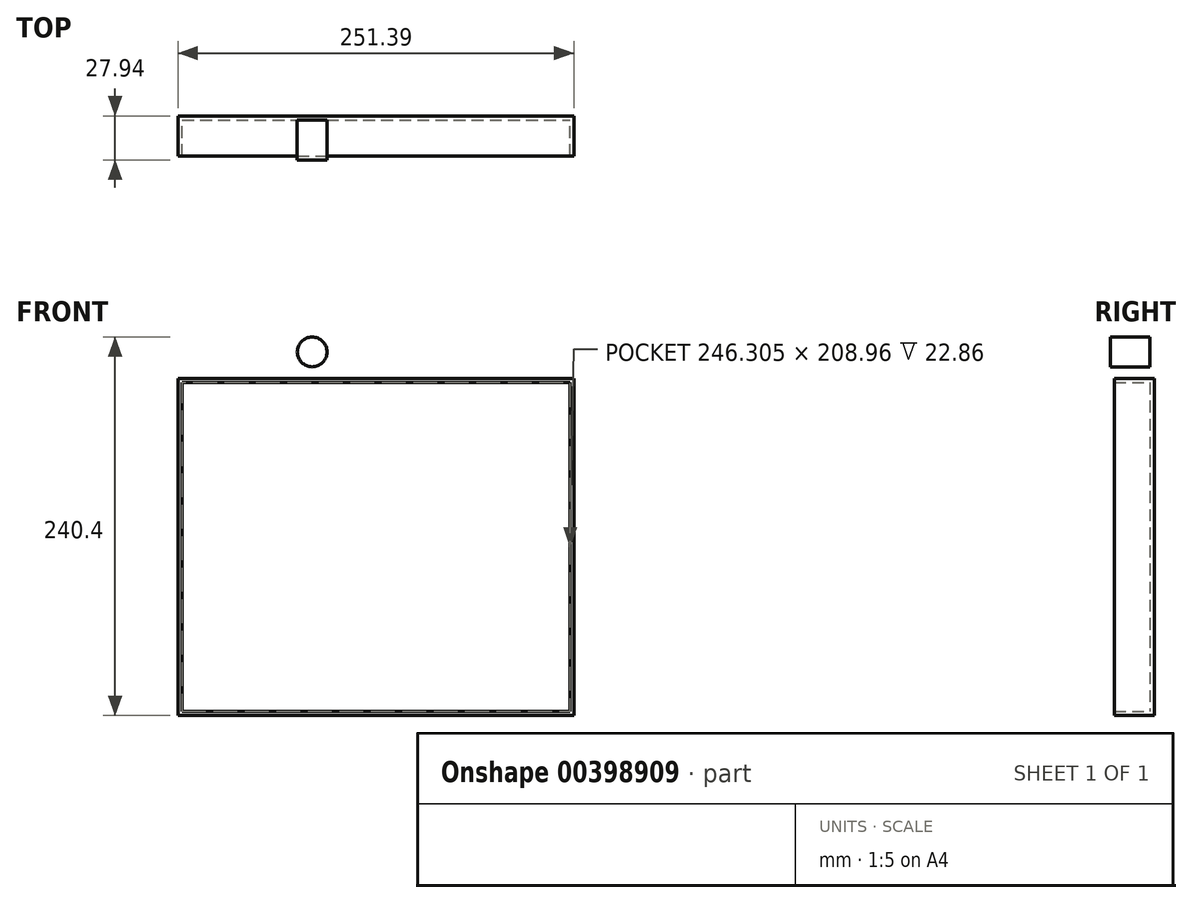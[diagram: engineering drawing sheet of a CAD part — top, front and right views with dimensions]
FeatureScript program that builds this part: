
annotation { "Feature Type Name" : "Feature", "Feature Type Description" : "" }
export const myFeature = defineFeature(function(context is Context, id is Id, definition is map)
    precondition{}
    {
        {
            var Q0;
            Q0=qCreatedBy(makeId("Front.planeOp"),FACE);
            var sketch = newSketch(context, id + "F0", { "sketchPlane" : qUnion([Q0])});
            skLineSegment(sketch, "E0.bottom", {"start": v(-605.9, 21.92) * mm, "end": v(-354.52, 21.92) * mm});
            skLineSegment(sketch, "E0.top", {"start": v(-605.9, -192.12) * mm, "end": v(-354.52, -192.12) * mm});
            skLineSegment(sketch, "E0.left", {"start": v(-605.9, 21.92) * mm, "end": v(-605.9, -192.12) * mm});
            skLineSegment(sketch, "E0.right", {"start": v(-354.52, 21.92) * mm, "end": v(-354.52, -192.12) * mm});
            skSolve(sketch);
        }
        {
            var Q0;
            Q0=makeQuery(id+"F0.imprint","IMPRINT",FACE,{"disambiguationData":[TD([[makeQuery(id+"F0.imprint","IMPRINT",EDGE,{"derivedFrom":sQuery(id+"F0.wireOp",EDGE,"E0.bottom")}),-1.0]])]});
            var sketch = newSketch(context, id + "F1", { "sketchPlane" : qUnion([Q0])});
            skLineSegment(sketch, "E1", {"start": v(-567.45, 7.98) * mm, "end": v(-581.38, -26.02) * mm});
            skLineSegment(sketch, "E2", {"start": v(-567.45, 7.98) * mm, "end": v(-552.4, -26.02) * mm});
            skLineSegment(sketch, "E3", {"start": v(-574.42, -9.02) * mm, "end": v(-559.92, -9.02) * mm});
            skLineSegment(sketch, "E4", {"start": v(-540.14, 7.98) * mm, "end": v(-540.14, -26.02) * mm});
            skLineSegment(sketch, "E5", {"start": v(-540.14, 7.98) * mm, "end": v(-517.28, -26.02) * mm});
            skLineSegment(sketch, "E6", {"start": v(-518.95, 7.98) * mm, "end": v(-517.28, -26.02) * mm});
            skLineSegment(sketch, "E7", {"start": v(-500, 7.98) * mm, "end": v(-500, -26.02) * mm});
            skFitSpline(sketch, "E8", {"points": [v(-500, 7.98) * mm, v(-476.6, -7.07) * mm, v(-500, -26.02) * mm], "startDerivative": vector(70.72, -29.12) * mm, "endDerivative": vector(-69.8, -38.82) * mm});
            skLineSegment(sketch, "E9", {"start": v(-466.56, 7.98) * mm, "end": v(-453.74, -9.86) * mm});
            skLineSegment(sketch, "E10", {"start": v(-453.74, -9.86) * mm, "end": v(-439.25, 10.77) * mm});
            skLineSegment(sketch, "E11", {"start": v(-439.25, 10.77) * mm, "end": v(-453.74, -9.86) * mm});
            skLineSegment(sketch, "E12", {"start": v(-453.74, -9.86) * mm, "end": v(-453.74, -26.58) * mm});
            skFitSpline(sketch, "E13", {"points": [v(-408.03, 9.1) * mm, v(-422.52, 0) * mm, v(-426.98, -24.35) * mm, v(-396.88, -24.9) * mm, v(-395.21, -9.86) * mm, v(-410.26, -9.3) * mm], "startDerivative": vector(-81.87, -29.83) * mm, "endDerivative": vector(-103.36, -22.07) * mm});
            skPoint(sketch, "E14", {"position": v(-382.4, -21.56) * mm});
            skLineSegment(sketch, "E15", {"start": v(-595.32, -62.8) * mm, "end": v(-595.32, -107.4) * mm});
            skLineSegment(sketch, "E16", {"start": v(-595.32, -85.1) * mm, "end": v(-572.46, -85.1) * mm});
            skLineSegment(sketch, "E17", {"start": v(-572.46, -85.1) * mm, "end": v(-572.46, -61.14) * mm});
            skLineSegment(sketch, "E18", {"start": v(-572.46, -85.1) * mm, "end": v(-572.46, -106.29) * mm});
            skLineSegment(sketch, "E19", {"start": v(-558.53, -61.14) * mm, "end": v(-566.33, -106.29) * mm});
            skLineSegment(sketch, "E20", {"start": v(-556.86, -59.46) * mm, "end": v(-552.4, -106.29) * mm});
            skLineSegment(sketch, "E21", {"start": v(-562.43, -83.71) * mm, "end": v(-554.55, -83.71) * mm});
            skLineSegment(sketch, "E22", {"start": v(-546.82, -61.14) * mm, "end": v(-546.82, -108.52) * mm});
            skLineSegment(sketch, "E23", {"start": v(-546.82, -61.14) * mm, "end": v(-531.22, -108.52) * mm});
            skLineSegment(sketch, "E24", {"start": v(-531.22, -108.52) * mm, "end": v(-531.22, -61.14) * mm});
            skLineSegment(sketch, "E25", {"start": v(-522.86, -61.7) * mm, "end": v(-522.86, -107.96) * mm});
            skFitSpline(sketch, "E26", {"points": [v(-522.86, -61.7) * mm, v(-505.02, -66.15) * mm, v(-502.79, -93.47) * mm, v(-522.86, -107.96) * mm], "startDerivative": vector(69.4, 1.67) * mm, "endDerivative": vector(-71.52, -29.11) * mm});
            skFitSpline(sketch, "E27", {"points": [v(-478.26, -61.7) * mm, v(-492.2, -61.7) * mm, v(-495.54, -80.09) * mm, v(-479.38, -86.78) * mm, v(-475.48, -98.48) * mm, v(-496.1, -107.96) * mm], "startDerivative": vector(-84.62, 26.35) * mm, "endDerivative": vector(-116.93, -28.25) * mm});
            skFitSpline(sketch, "E28", {"points": [v(-459.87, -61.7) * mm, v(-471.02, -80.09) * mm, v(-466, -107.96) * mm, v(-447.05, -107.96) * mm, v(-437.02, -73.4) * mm, v(-450.4, -61.7) * mm, v(-459.87, -61.7) * mm]});
            skLineSegment(sketch, "E29", {"start": v(-427.54, -61.7) * mm, "end": v(-433.12, -107.4) * mm});
            skLineSegment(sketch, "E30", {"start": v(-427.54, -61.7) * mm, "end": v(-419.74, -107.4) * mm});
            skLineSegment(sketch, "E31", {"start": v(-419.74, -107.4) * mm, "end": v(-408.03, -61.7) * mm});
            skLineSegment(sketch, "E32", {"start": v(-408.03, -61.7) * mm, "end": v(-401.34, -107.4) * mm});
            skLineSegment(sketch, "E33", {"start": v(-390.2, -61.7) * mm, "end": v(-390.2, -107.4) * mm});
            skLineSegment(sketch, "E34", {"start": v(-390.2, -61.7) * mm, "end": v(-364.18, -64.87) * mm});
            skLineSegment(sketch, "E35", {"start": v(-390.2, -84.55) * mm, "end": v(-364.18, -87.72) * mm});
            skLineSegment(sketch, "E36", {"start": v(-390.2, -107.4) * mm, "end": v(-362.33, -107.4) * mm});
            skLineSegment(sketch, "E37", {"start": v(-595.32, -127.47) * mm, "end": v(-600.33, -172.06) * mm});
            skLineSegment(sketch, "E38", {"start": v(-595.32, -127.47) * mm, "end": v(-587.51, -172.06) * mm});
            skLineSegment(sketch, "E39", {"start": v(-587.51, -172.06) * mm, "end": v(-578.04, -127.47) * mm});
            skLineSegment(sketch, "E40", {"start": v(-578.04, -127.47) * mm, "end": v(-570.23, -172.06) * mm});
            skLineSegment(sketch, "E41", {"start": v(-557.97, -126.9) * mm, "end": v(-563.55, -169.83) * mm});
            skLineSegment(sketch, "E42", {"start": v(-563.55, -169.83) * mm, "end": v(-557.97, -126.9) * mm});
            skLineSegment(sketch, "E43", {"start": v(-557.97, -126.9) * mm, "end": v(-546.82, -170.39) * mm});
            skLineSegment(sketch, "E44", {"start": v(-560.76, -148.37) * mm, "end": v(-552.18, -149.48) * mm});
            skLineSegment(sketch, "E45", {"start": v(-537.9, -130.25) * mm, "end": v(-537.9, -168.71) * mm});
            skLineSegment(sketch, "E46", {"start": v(-537.9, -130.25) * mm, "end": v(-520.63, -168.71) * mm});
            skLineSegment(sketch, "E47", {"start": v(-520.63, -168.71) * mm, "end": v(-515.6, -130.25) * mm});
            skLineSegment(sketch, "E48", {"start": v(-486.63, -130.25) * mm, "end": v(-486.63, -175.96) * mm});
            skLineSegment(sketch, "E49", {"start": v(-462.1, -130.25) * mm, "end": v(-462.1, -175.96) * mm});
            skLineSegment(sketch, "E50", {"start": v(-493.87, -142.52) * mm, "end": v(-452.07, -142.52) * mm});
            skLineSegment(sketch, "E51", {"start": v(-494.43, -167.04) * mm, "end": v(-450.4, -167.04) * mm});
            skLineSegment(sketch, "E52", {"start": v(-424.75, -135.83) * mm, "end": v(-419.18, -129.14) * mm});
            skLineSegment(sketch, "E53", {"start": v(-419.18, -129.14) * mm, "end": v(-419.18, -173.17) * mm});
            skLineSegment(sketch, "E54", {"start": v(-419.18, -173.17) * mm, "end": v(-430.89, -173.17) * mm});
            skLineSegment(sketch, "E55", {"start": v(-430.89, -173.17) * mm, "end": v(-408.03, -173.17) * mm});
            skLineSegment(sketch, "E56", {"start": v(-390.2, -135.27) * mm, "end": v(-385.09, -129.14) * mm});
            skLineSegment(sketch, "E57", {"start": v(-385.09, -129.14) * mm, "end": v(-385.09, -173.17) * mm});
            skLineSegment(sketch, "E58", {"start": v(-385.09, -173.17) * mm, "end": v(-395.21, -173.17) * mm});
            skLineSegment(sketch, "E59", {"start": v(-395.21, -173.17) * mm, "end": v(-371.24, -173.17) * mm});
            skLineSegment(sketch, "E60", {"start": v(-581.38, -26.02) * mm, "end": v(-577.86, -26.02) * mm});
            skLineSegment(sketch, "E61", {"start": v(-577.86, -26.02) * mm, "end": v(-573.29, -11.6) * mm});
            skLineSegment(sketch, "E62", {"start": v(-573.29, -11.6) * mm, "end": v(-561.68, -11.6) * mm});
            skLineSegment(sketch, "E63", {"start": v(-561.68, -11.6) * mm, "end": v(-555.59, -26.02) * mm});
            skLineSegment(sketch, "E64", {"start": v(-555.59, -26.02) * mm, "end": v(-552.4, -26.02) * mm});
            skLineSegment(sketch, "E65", {"start": v(-540.14, -26.02) * mm, "end": v(-543.16, -26.02) * mm});
            skLineSegment(sketch, "E66", {"start": v(-543.16, -26.02) * mm, "end": v(-543.16, 14.43) * mm});
            skLineSegment(sketch, "E67", {"start": v(-543.16, 14.43) * mm, "end": v(-520.54, -15.82) * mm});
            skLineSegment(sketch, "E68", {"start": v(-520.54, -15.82) * mm, "end": v(-522.41, 8.21) * mm});
            skLineSegment(sketch, "E69", {"start": v(-522.41, 8.21) * mm, "end": v(-518.95, 7.98) * mm});
            skLineSegment(sketch, "E70", {"start": v(-498.14, 4) * mm, "end": v(-498.14, -19.57) * mm});
            skFitSpline(sketch, "E71", {"points": [v(-498.14, 4) * mm, v(-493.1, 2.12) * mm, v(-486.77, -3.28) * mm, v(-485.13, -11.95) * mm, v(-489.35, -17.23) * mm, v(-498.14, -19.57) * mm], "startDerivative": vector(28.92, -8.7) * mm, "endDerivative": vector(-43.56, -6.88) * mm});
            skSolve(sketch);
        }
        {
            var Q0;
            Q0=makeQuery(id+"F0.imprint","IMPRINT",FACE,{"disambiguationData":[TD([[makeQuery(id+"F0.imprint","IMPRINT",EDGE,{"derivedFrom":sQuery(id+"F0.wireOp",EDGE,"E0.bottom")}),-1.0]])]});
            extrude(context, id + "F2", {"entities" : qUnion([Q0]), "depth" : 25.4 * mm});
        }
        {
            var Q0;
            Q0=makeQuery(id+"F2.opExtrude","CAP_FACE",FACE,{"disambiguationData":[OSD([sQuery(id+"F0.wireOp",EDGE,"E0.bottom"),sQuery(id+"F0.wireOp",EDGE,"E0.top"),sQuery(id+"F0.wireOp",EDGE,"E0.left"),sQuery(id+"F0.wireOp",EDGE,"E0.right")])],"isStart":false});
            shell(context, id + "F3", {"entities" : qUnion([Q0]), "thickness" : 2.54 * mm});
        }
        {
            var Q0;
            Q0=makeQuery(id+"F3.opShell","OFFSET_FACE",FACE,{"disambiguationData":[OSD([sQuery(id+"F0.wireOp",EDGE,"E0.bottom"),sQuery(id+"F0.wireOp",EDGE,"E0.top"),sQuery(id+"F0.wireOp",EDGE,"E0.left"),sQuery(id+"F0.wireOp",EDGE,"E0.right")])]});
            var sketch = newSketch(context, id + "F4", { "sketchPlane" : qUnion([Q0])});
            skCircle(sketch, "E72", {"center": v(-520.73, 38.84) * mm, "radius": 9.44 * mm});
            skSolve(sketch);
        }
        {
            var Q0;
            Q0 = qSketchRegion(id + "F4", true);
            extrude(context, id + "F5", {"entities" : qUnion([Q0]), "depth" : 25.4 * mm});
        }
        {
            var Q0;
            Q0=makeQuery(id+"F3.opShell","OFFSET_FACE",FACE,{"disambiguationData":[OSD([sQuery(id+"F0.wireOp",EDGE,"E0.bottom"),sQuery(id+"F0.wireOp",EDGE,"E0.top"),sQuery(id+"F0.wireOp",EDGE,"E0.left"),sQuery(id+"F0.wireOp",EDGE,"E0.right")])]});
            var sketch = newSketch(context, id + "F6", { "sketchPlane" : qUnion([Q0])});
            skSolve(sketch);
        }
        {
            var Q0;
            Q0=sQuery(id+"F1.wireOp",EDGE,"E66");
            extrude(context, id + "F7", {"bodyType" : ToolBodyType.SURFACE, "surfaceEntities" : qUnion([Q0]), "depth" : 25.4 * mm});
        }
    });
